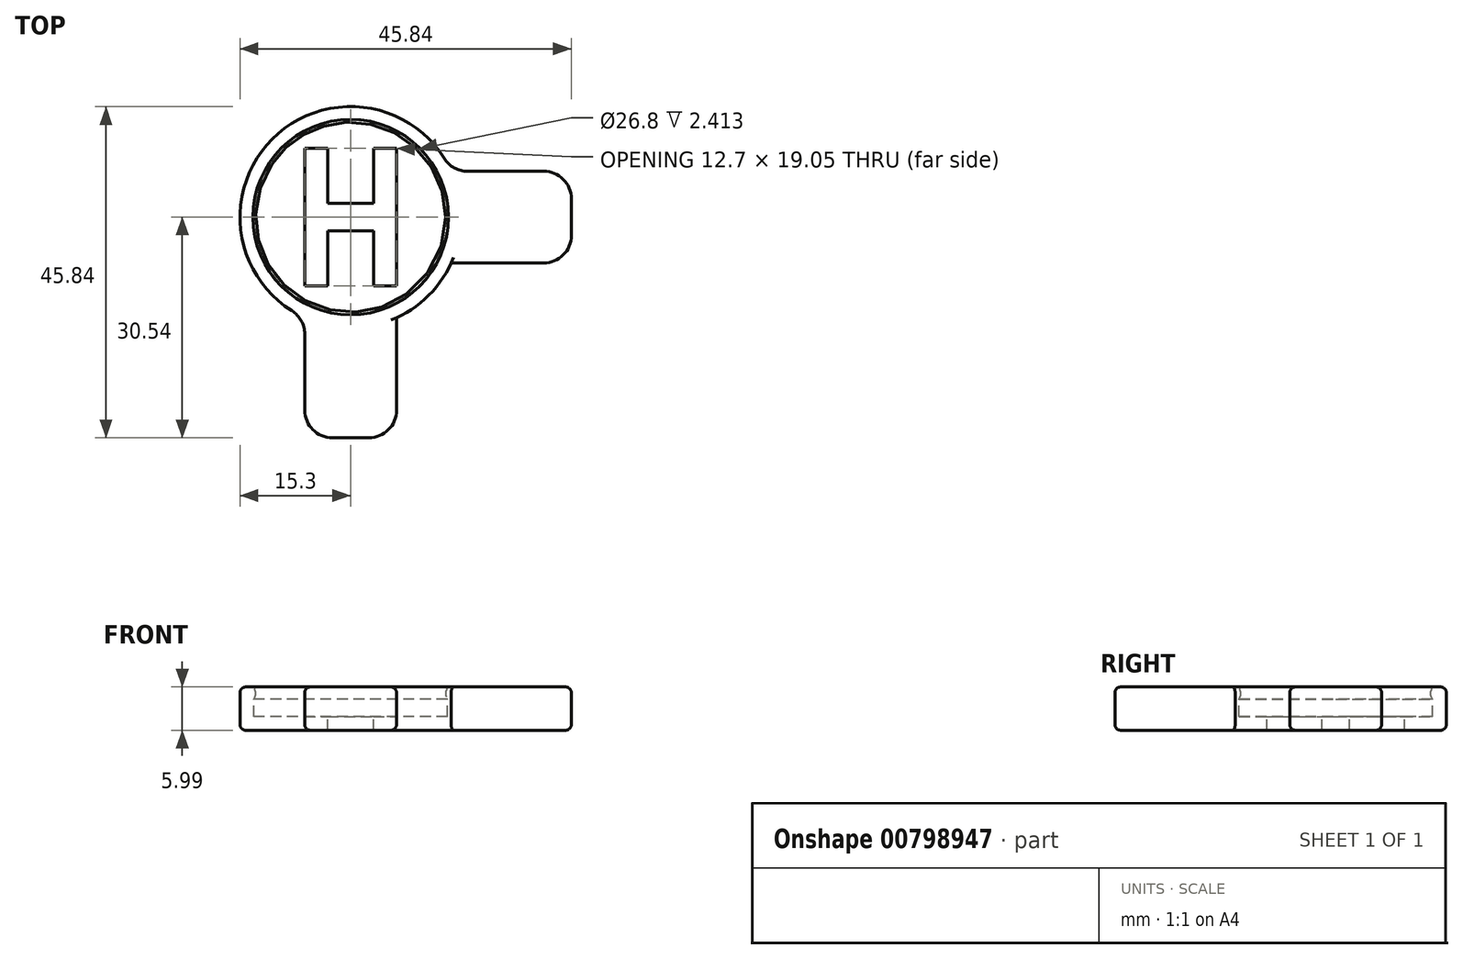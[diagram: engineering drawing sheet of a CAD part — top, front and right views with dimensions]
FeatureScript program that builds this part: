
annotation { "Feature Type Name" : "Feature", "Feature Type Description" : "" }
export const myFeature = defineFeature(function(context is Context, id is Id, definition is map)
    precondition{}
    {
        {
            var Q0;
            Q0=qCreatedBy(makeId("Front.planeOp"),FACE);
            var sketch = newSketch(context, id + "F0", { "sketchPlane" : qUnion([Q0])});
            skLineSegment(sketch, "E0", {"start": v(15.3, 4.17) * mm, "end": v(15.3, 0) * mm});
            skLineSegment(sketch, "E1", {"start": v(15.3, 0) * mm, "end": v(0, 0) * mm});
            skArc(sketch, "E2", {"start": v(15.3, 4.17) * mm, "mid": v(13.5, 4.2) * mm, "end": v(13.53, 5.99) * mm});
            skLineSegment(sketch, "E3", {"start": v(0, 10.9) * mm, "end": v(0, -2.45) * mm, "construction": true});
            skLineSegment(sketch, "E4", {"start": v(0, 0) * mm, "end": v(0, 1.9) * mm});
            skLineSegment(sketch, "E5", {"start": v(0, 1.9) * mm, "end": v(13.4, 1.9) * mm});
            skLineSegment(sketch, "E6", {"start": v(13.4, 1.9) * mm, "end": v(13.4, 4.32) * mm});
            skLineSegment(sketch, "E7", {"start": v(15.3, 4.17) * mm, "end": v(15.3, 5.99) * mm});
            skLineSegment(sketch, "E8", {"start": v(15.3, 5.99) * mm, "end": v(13.53, 5.99) * mm});
            skSolve(sketch);
        }
        {
            var Q0;
            Q0=qSketchRegion(id+"F0",true);
            var Q1;
            Q1=sQuery(id+"F0.wireOp",EDGE,"E3");
            revolve(context, id + "F1", {"surfaceOperationType" : NewSurfaceOperationType.NEW, "entities" : qUnion([Q0]), "axis" : qUnion([Q1]), "revolveType" : RevolveType.FULL});
        }
        {
            var Q0;
            Q0=makeQuery(id+"F1.opRevolve","SWEPT_FACE",FACE,{"disambiguationData":[OSD([sQuery(id+"F0.wireOp",EDGE,"E8")])]});
            var sketch = newSketch(context, id + "F2", { "sketchPlane" : qUnion([Q0])});
            skLineSegment(sketch, "E9.bottom", {"start": v(30.54, 6.35) * mm, "end": v(13.92, 6.35) * mm});
            skLineSegment(sketch, "E9.top", {"start": v(30.54, -6.35) * mm, "end": v(13.92, -6.35) * mm});
            skLineSegment(sketch, "E9.left", {"start": v(30.54, 6.35) * mm, "end": v(30.54, -6.35) * mm});
            skLineSegment(sketch, "E10.bottom", {"start": v(6.35, -30.54) * mm, "end": v(-6.35, -30.54) * mm});
            skLineSegment(sketch, "E10.left", {"start": v(6.35, -30.54) * mm, "end": v(6.35, -13.92) * mm});
            skLineSegment(sketch, "E10.right", {"start": v(-6.35, -30.54) * mm, "end": v(-6.35, -13.92) * mm});
            skArc(sketch, "E11.0", {"start": v(-6.35, -13.92) * mm, "mid": v(0, -15.3) * mm, "end": v(6.35, -13.92) * mm});
            skArc(sketch, "E12.trimOffspring", {"start": v(13.92, -6.35) * mm, "mid": v(15.3, 0) * mm, "end": v(13.92, 6.35) * mm});
            skSolve(sketch);
        }
        {
            var Q0;
            Q0=qSketchRegion(id+"F2",true);
            var Q1;
            Q1=makeQuery(id+"F1.opRevolve","SWEPT_FACE",FACE,{"disambiguationData":[OSD([sQuery(id+"F0.wireOp",EDGE,"E1")])]});
            extrude(context, id + "F3", {"entities" : qUnion([Q0]), "operationType" : NewBodyOperationType.ADD, "endBound" : BoundingType.UP_TO_SURFACE, "oppositeDirection" : true, "depth" : 25.4 * mm, "endBoundEntityFace" : qUnion([Q1]), "offsetDistance" : 25.4 * mm});
        }
        {
            var Q0;
            Q0=makeQuery(id+"F3.opExtrude","SWEPT_EDGE",EDGE,{"disambiguationData":[OSD([sQuery(id+"F2.wireOp",EDGE,"E10.bottom"),sQuery(id+"F2.wireOp",EDGE,"E10.right")])]});
            var Q1;
            Q1=makeQuery(id+"F3.opExtrude","SWEPT_EDGE",EDGE,{"disambiguationData":[OSD([sQuery(id+"F0.wireOp",EDGE,"E7"),sQuery(id+"F0.wireOp",EDGE,"E8"),sQuery(id+"F2.wireOp",EDGE,"E10.right"),sQuery(id+"F2.wireOp",EDGE,"E11.0")])]});
            var Q2;
            Q2=makeQuery(id+"F3.opExtrude","SWEPT_EDGE",EDGE,{"disambiguationData":[OSD([sQuery(id+"F2.wireOp",EDGE,"E10.bottom"),sQuery(id+"F2.wireOp",EDGE,"E10.left")])]});
            var Q3;
            Q3=makeQuery(id+"F3.opExtrude","SWEPT_EDGE",EDGE,{"disambiguationData":[OSD([sQuery(id+"F0.wireOp",EDGE,"E7"),sQuery(id+"F0.wireOp",EDGE,"E8"),sQuery(id+"F2.wireOp",EDGE,"E10.left"),sQuery(id+"F2.wireOp",EDGE,"E11.0")])]});
            var Q4;
            Q4=makeQuery(id+"F3.opExtrude","SWEPT_EDGE",EDGE,{"disambiguationData":[OSD([sQuery(id+"F0.wireOp",EDGE,"E7"),sQuery(id+"F0.wireOp",EDGE,"E8"),sQuery(id+"F2.wireOp",EDGE,"E9.top"),sQuery(id+"F2.wireOp",EDGE,"E12.trimOffspring")])]});
            var Q5;
            Q5=makeQuery(id+"F3.opExtrude","SWEPT_EDGE",EDGE,{"disambiguationData":[OSD([sQuery(id+"F2.wireOp",EDGE,"E9.top"),sQuery(id+"F2.wireOp",EDGE,"E9.left")])]});
            var Q6;
            Q6=makeQuery(id+"F3.opExtrude","SWEPT_EDGE",EDGE,{"disambiguationData":[OSD([sQuery(id+"F2.wireOp",EDGE,"E9.bottom"),sQuery(id+"F2.wireOp",EDGE,"E9.left")])]});
            var Q7;
            Q7=makeQuery(id+"F3.opExtrude","SWEPT_EDGE",EDGE,{"disambiguationData":[OSD([sQuery(id+"F0.wireOp",EDGE,"E7"),sQuery(id+"F0.wireOp",EDGE,"E8"),sQuery(id+"F2.wireOp",EDGE,"E9.bottom"),sQuery(id+"F2.wireOp",EDGE,"E12.trimOffspring")])]});
            fillet(context, id + "F4", {"entities" : qUnion([Q0, Q1, Q2, Q3, Q4, Q5, Q6, Q7]), "radius" : 3.8 * mm, "tangentPropagation" : true, "allowEdgeOverflow" : false});
        }
        {
            var Q0;
            Q0=makeQuery(id+"F3.opExtrude","CAP_EDGE",EDGE,{"disambiguationData":[OSD([sQuery(id+"F2.wireOp",EDGE,"E10.bottom")])],"isStart":true});
            var Q1;
            Q1=makeQuery(id+"F3.opExtrude","CAP_EDGE",EDGE,{"disambiguationData":[OSD([sQuery(id+"F2.wireOp",EDGE,"E10.bottom")])],"isStart":false});
            fillet(context, id + "F5", {"entities" : qUnion([Q0, Q1]), "radius" : 0.76 * mm, "tangentPropagation" : true, "allowEdgeOverflow" : false});
        }
        {
            var Q0;
            Q0=makeQuery(id+"F1.opRevolve","SWEPT_FACE",FACE,{"disambiguationData":[OSD([sQuery(id+"F0.wireOp",EDGE,"E5")])]});
            var sketch = newSketch(context, id + "F6", { "sketchPlane" : qUnion([Q0])});
            skLineSegment(sketch, "E13", {"start": v(-6.35, 9.52) * mm, "end": v(-3.17, 9.52) * mm});
            skLineSegment(sketch, "E14", {"start": v(-3.17, 9.52) * mm, "end": v(-3.17, 1.9) * mm});
            skLineSegment(sketch, "E15", {"start": v(-3.17, 1.9) * mm, "end": v(3.18, 1.9) * mm});
            skLineSegment(sketch, "E16", {"start": v(3.18, 1.9) * mm, "end": v(3.18, 9.53) * mm});
            skLineSegment(sketch, "E17", {"start": v(3.17, 9.53) * mm, "end": v(6.35, 9.53) * mm});
            skLineSegment(sketch, "E18", {"start": v(6.35, 9.52) * mm, "end": v(6.35, -9.52) * mm});
            skLineSegment(sketch, "E19", {"start": v(6.35, -9.52) * mm, "end": v(3.18, -9.52) * mm});
            skLineSegment(sketch, "E20", {"start": v(3.18, -9.52) * mm, "end": v(3.18, -1.9) * mm});
            skLineSegment(sketch, "E21", {"start": v(3.18, -1.9) * mm, "end": v(-3.18, -1.9) * mm});
            skLineSegment(sketch, "E22", {"start": v(-3.18, -1.9) * mm, "end": v(-3.17, -9.53) * mm});
            skLineSegment(sketch, "E23", {"start": v(-3.17, -9.53) * mm, "end": v(-6.35, -9.53) * mm});
            skLineSegment(sketch, "E24", {"start": v(-6.35, -9.53) * mm, "end": v(-6.35, 9.52) * mm});
            skSolve(sketch);
        }
        {
            var Q0;
            Q0 = qSketchRegion(id + "F6", true);
            extrude(context, id + "F7", {"entities" : qUnion([Q0]), "operationType" : NewBodyOperationType.REMOVE, "oppositeDirection" : true, "depth" : 25.4 * mm, "offsetDistance" : 25.4 * mm});
        }
    });
